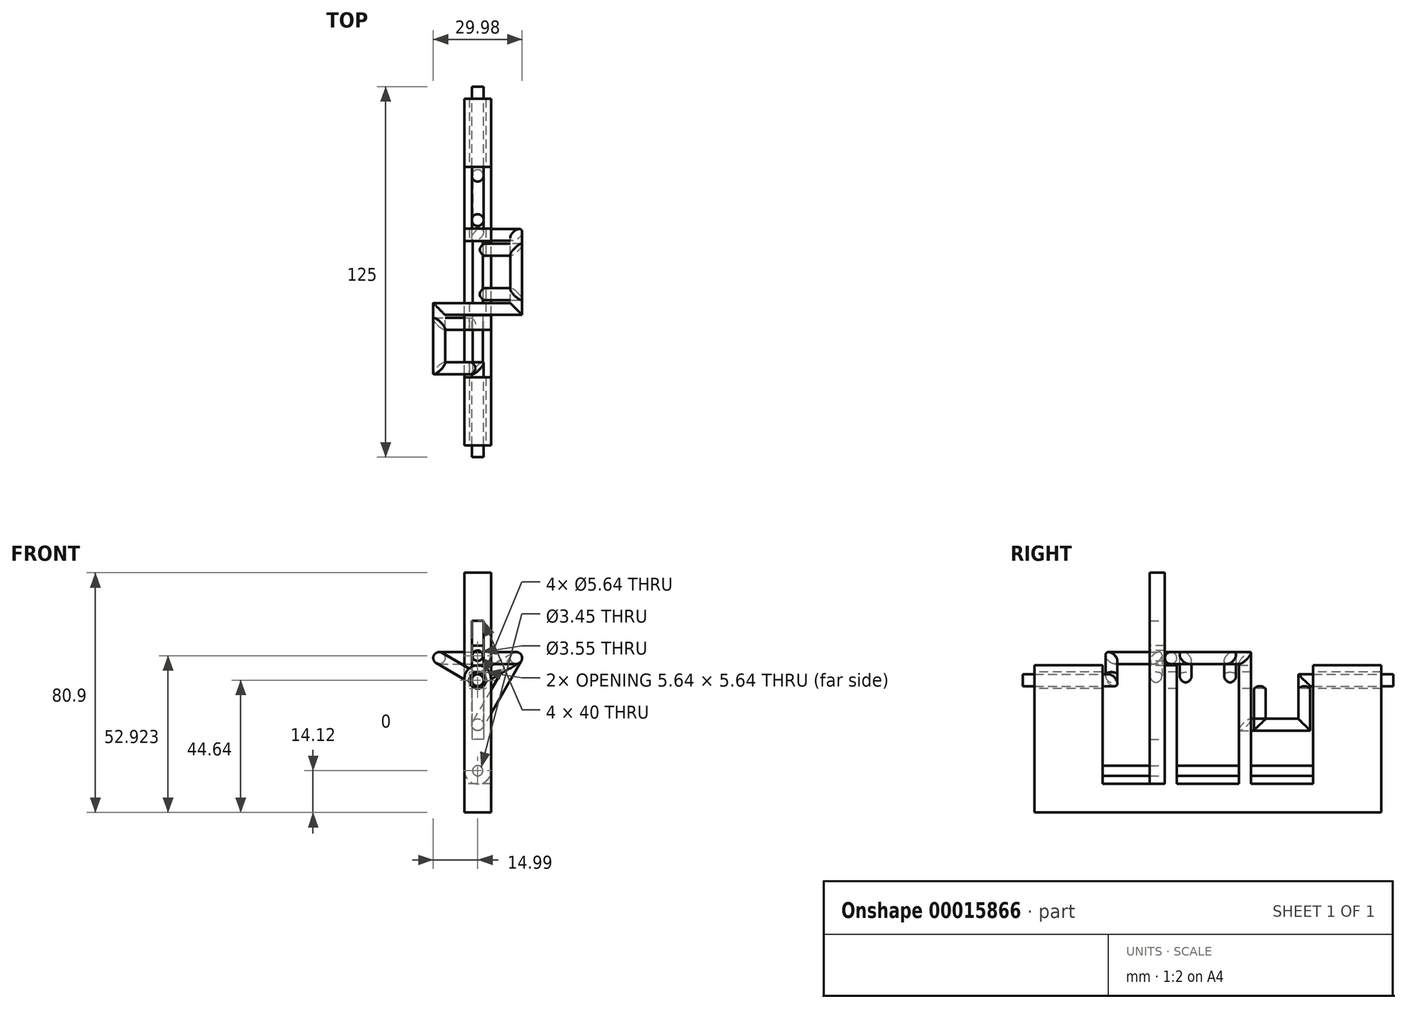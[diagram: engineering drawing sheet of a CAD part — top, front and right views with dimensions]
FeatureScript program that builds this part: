
annotation { "Feature Type Name" : "Feature", "Feature Type Description" : "" }
export const myFeature = defineFeature(function(context is Context, id is Id, definition is map)
    precondition{}
    {
        {
            var Q0;
            Q0=qCreatedBy(makeId("Front.planeOp"),FACE);
            var sketch = newSketch(context, id + "F0", { "sketchPlane" : qUnion([Q0])});
            skCircle(sketch, "E0", {"center": v(0, 0) * mm, "radius": 2 * mm});
            skLineSegment(sketch, "E1", {"start": v(0, 0) * mm, "end": v(-13, 7.5) * mm, "construction": true});
            skLineSegment(sketch, "E2", {"start": v(0, 0) * mm, "end": v(13, 7.5) * mm, "construction": true});
            skLineSegment(sketch, "E3", {"start": v(0, 0) * mm, "end": v(0, -15) * mm, "construction": true});
            skSolve(sketch);
        }
        {
            var Q0;
            Q0=qCreatedBy(makeId("Top.planeOp"),FACE);
            var sketch = newSketch(context, id + "F1", { "sketchPlane" : qUnion([Q0])});
            skLineSegment(sketch, "E4", {"start": v(0, 0) * mm, "end": v(0, 30) * mm});
            skLineSegment(sketch, "E5", {"start": v(0, 45) * mm, "end": v(0, 55) * mm});
            skLineSegment(sketch, "E6", {"start": v(0, 70) * mm, "end": v(0, 80) * mm});
            skLineSegment(sketch, "E7", {"start": v(0, 95) * mm, "end": v(0, 125) * mm});
            skLineSegment(sketch, "E8", {"start": v(0, 30) * mm, "end": v(0, 45) * mm, "construction": true});
            skLineSegment(sketch, "E9", {"start": v(0, 55) * mm, "end": v(0, 70) * mm, "construction": true});
            skLineSegment(sketch, "E10", {"start": v(0, 80) * mm, "end": v(0, 95) * mm, "construction": true});
            skSolve(sketch);
        }
        {
            var Q0;
            Q0=sQuery(id+"F0.wireOp",VERTEX,"E1.end");
            var Q1;
            Q1=sQuery(id+"F0.wireOp",VERTEX,"E2.start");
            var Q2;
            Q2=sQuery(id+"F1.wireOp",VERTEX,"E8.start");
            cPlane(context, id + "F2", {"entities" : qUnion([Q0, Q1, Q2]), "cplaneType" : CPlaneType.THREE_POINT, "offset" : 150 * mm, "width" : 150 * mm, "height" : 150 * mm});
        }
        {
            var Q0;
            Q0=sQuery(id+"F0.wireOp",VERTEX,"E2.end");
            var Q1;
            Q1=sQuery(id+"F0.wireOp",VERTEX,"E2.start");
            var Q2;
            Q2=sQuery(id+"F1.wireOp",VERTEX,"E8.start");
            cPlane(context, id + "F3", {"entities" : qUnion([Q0, Q1, Q2]), "cplaneType" : CPlaneType.THREE_POINT, "offset" : 150 * mm, "width" : 150 * mm, "height" : 150 * mm});
        }
        {
            var Q0;
            Q0=qCreatedBy(id+"F2.planeOp",FACE);
            var sketch = newSketch(context, id + "F4", { "sketchPlane" : qUnion([Q0])});
            skLineSegment(sketch, "E11.0", {"start": v(0, 0) * mm, "end": v(-15, 0) * mm, "construction": true});
            skLineSegment(sketch, "E12.0", {"start": v(0, -30) * mm, "end": v(0, -45) * mm, "construction": true});
            skLineSegment(sketch, "E13", {"start": v(0, -30) * mm, "end": v(-15, -30) * mm});
            skLineSegment(sketch, "E14", {"start": v(-15, -30) * mm, "end": v(-15, -45) * mm});
            skLineSegment(sketch, "E15", {"start": v(-15, -45) * mm, "end": v(0, -45) * mm});
            skSolve(sketch);
        }
        {
            var Q0;
            Q0=qCreatedBy(id+"F3.planeOp",FACE);
            var sketch = newSketch(context, id + "F5", { "sketchPlane" : qUnion([Q0])});
            skLineSegment(sketch, "E16.0", {"start": v(0, 0) * mm, "end": v(15, 0) * mm, "construction": true});
            skLineSegment(sketch, "E16.1", {"start": v(0, 55) * mm, "end": v(0, 70) * mm, "construction": true});
            skLineSegment(sketch, "E17", {"start": v(0, 55) * mm, "end": v(15, 55) * mm});
            skLineSegment(sketch, "E18", {"start": v(15, 55) * mm, "end": v(15, 70) * mm});
            skLineSegment(sketch, "E19", {"start": v(15, 70) * mm, "end": v(0, 70) * mm});
            skSolve(sketch);
        }
        {
            var Q0;
            Q0=qCreatedBy(makeId("Right.planeOp"),FACE);
            var sketch = newSketch(context, id + "F6", { "sketchPlane" : qUnion([Q0])});
            skLineSegment(sketch, "E20.0", {"start": v(0, 0) * mm, "end": v(0, -15) * mm, "construction": true});
            skLineSegment(sketch, "E20.1", {"start": v(80, 0) * mm, "end": v(95, 0) * mm, "construction": true});
            skLineSegment(sketch, "E21", {"start": v(80, 0) * mm, "end": v(80, -15) * mm});
            skLineSegment(sketch, "E22", {"start": v(80, -15) * mm, "end": v(95, -15) * mm});
            skLineSegment(sketch, "E23", {"start": v(95, -15) * mm, "end": v(95, 0) * mm});
            skSolve(sketch);
        }
        {
            var Q0;
            Q0=makeQuery(id+"F0.imprint","IMPRINT",FACE,{"disambiguationData":[TD([[makeQuery(id+"F0.imprint","IMPRINT",EDGE,{"derivedFrom":sQuery(id+"F0.wireOp",EDGE,"E0")}),1.0]])]});
            var Q1;
            Q1=sQuery(id+"F1.wireOp",EDGE,"E4");
            var Q2;
            Q2=sQuery(id+"F4.wireOp",EDGE,"E13");
            var Q3;
            Q3=sQuery(id+"F4.wireOp",EDGE,"E14");
            var Q4;
            Q4=sQuery(id+"F4.wireOp",EDGE,"E15");
            var Q5;
            Q5=sQuery(id+"F1.wireOp",EDGE,"E5");
            var Q6;
            Q6=sQuery(id+"F5.wireOp",EDGE,"E17");
            var Q7;
            Q7=sQuery(id+"F5.wireOp",EDGE,"E19");
            var Q8;
            Q8=sQuery(id+"F5.wireOp",EDGE,"E18");
            var Q9;
            Q9=sQuery(id+"F1.wireOp",EDGE,"E6");
            var Q10;
            Q10=sQuery(id+"F6.wireOp",EDGE,"E21");
            var Q11;
            Q11=sQuery(id+"F6.wireOp",EDGE,"E22");
            var Q12;
            Q12=sQuery(id+"F6.wireOp",EDGE,"E23");
            var Q13;
            Q13=sQuery(id+"F1.wireOp",EDGE,"E7");
            sweep(context, id + "F7", {"profiles" : qUnion([Q0]), "path" : qUnion([Q1, Q2, Q3, Q4, Q5, Q6, Q7, Q8, Q9, Q10, Q11, Q12, Q13])});
        }
        {
            var Q0;
            Q0=qCreatedBy(makeId("Right.planeOp"),FACE);
            var sketch = newSketch(context, id + "F8", { "sketchPlane" : qUnion([Q0])});
            skLineSegment(sketch, "E24", {"start": v(4, -44.64) * mm, "end": v(4, 5) * mm});
            skLineSegment(sketch, "E25", {"start": v(4, 5) * mm, "end": v(27, 5) * mm});
            skLineSegment(sketch, "E26", {"start": v(27, 5) * mm, "end": v(27, -35) * mm});
            skLineSegment(sketch, "E27", {"start": v(27, -35) * mm, "end": v(47.92, -35) * mm});
            skLineSegment(sketch, "E28", {"start": v(47.92, -35) * mm, "end": v(47.92, 5) * mm});
            skLineSegment(sketch, "E29", {"start": v(47.92, 5) * mm, "end": v(52.04, 5) * mm});
            skLineSegment(sketch, "E30", {"start": v(52.04, 5) * mm, "end": v(52.04, -35) * mm});
            skLineSegment(sketch, "E31", {"start": v(52.04, -35) * mm, "end": v(72.96, -35) * mm});
            skLineSegment(sketch, "E32", {"start": v(72.96, -35) * mm, "end": v(72.96, 5) * mm});
            skLineSegment(sketch, "E33", {"start": v(72.96, 5) * mm, "end": v(77.08, 5) * mm});
            skLineSegment(sketch, "E34", {"start": v(77.08, 5) * mm, "end": v(77.08, -35) * mm});
            skLineSegment(sketch, "E35", {"start": v(77.08, -35) * mm, "end": v(98, -35) * mm});
            skLineSegment(sketch, "E36", {"start": v(98, -35) * mm, "end": v(98, 5) * mm});
            skLineSegment(sketch, "E37", {"start": v(98, 5) * mm, "end": v(121, 5) * mm});
            skLineSegment(sketch, "E38", {"start": v(121, 5) * mm, "end": v(121, -44.64) * mm});
            skLineSegment(sketch, "E39", {"start": v(121, -44.64) * mm, "end": v(4, -44.64) * mm});
            skSolve(sketch);
        }
        {
            var Q0;
            Q0=makeQuery(id+"F8.imprint","IMPRINT",FACE,{"disambiguationData":[TD([[makeQuery(id+"F8.imprint","IMPRINT",EDGE,{"derivedFrom":sQuery(id+"F8.wireOp",EDGE,"E24")}),-1.0]])]});
            extrude(context, id + "F9", {"entities" : qUnion([Q0]), "endBound" : BoundingType.SYMMETRIC, "depth" : 9 * mm});
        }
        {
            var Q0;
            Q0=makeQuery(id+"F9.opExtrude","SWEPT_FACE",FACE,{"disambiguationData":[OSD([sQuery(id+"F8.wireOp",EDGE,"E24")])]});
            var sketch = newSketch(context, id + "F10", { "sketchPlane" : qUnion([Q0])});
            skCircle(sketch, "E40", {"center": v(0, 0) * mm, "radius": 2.82 * mm});
            skSolve(sketch);
        }
        {
            var Q0;
            Q0=makeQuery(id+"F9.opExtrude","CAP_FACE",FACE,{"disambiguationData":[OSD([sQuery(id+"F8.wireOp",EDGE,"E24"),sQuery(id+"F8.wireOp",EDGE,"E25"),sQuery(id+"F8.wireOp",EDGE,"E26"),sQuery(id+"F8.wireOp",EDGE,"E27"),sQuery(id+"F8.wireOp",EDGE,"E28"),sQuery(id+"F8.wireOp",EDGE,"E29"),sQuery(id+"F8.wireOp",EDGE,"E30"),sQuery(id+"F8.wireOp",EDGE,"E31"),sQuery(id+"F8.wireOp",EDGE,"E32"),sQuery(id+"F8.wireOp",EDGE,"E33"),sQuery(id+"F8.wireOp",EDGE,"E34"),sQuery(id+"F8.wireOp",EDGE,"E35"),sQuery(id+"F8.wireOp",EDGE,"E36"),sQuery(id+"F8.wireOp",EDGE,"E37"),sQuery(id+"F8.wireOp",EDGE,"E38"),sQuery(id+"F8.wireOp",EDGE,"E39")])],"isStart":false});
            var sketch = newSketch(context, id + "F11", { "sketchPlane" : qUnion([Q0])});
            skLineSegment(sketch, "E41.0.0", {"start": v(4, 5) * mm, "end": v(4, -44.64) * mm});
            skLineSegment(sketch, "E41.0.1", {"start": v(4, -44.64) * mm, "end": v(121, -44.64) * mm});
            skLineSegment(sketch, "E41.0.2", {"start": v(121, -44.64) * mm, "end": v(121, 5) * mm});
            skLineSegment(sketch, "E41.0.3", {"start": v(121, 5) * mm, "end": v(98, 5) * mm});
            skLineSegment(sketch, "E41.0.4", {"start": v(98, 5) * mm, "end": v(98, -35) * mm});
            skLineSegment(sketch, "E41.0.5", {"start": v(98, -35) * mm, "end": v(77.08, -35) * mm});
            skLineSegment(sketch, "E41.0.6", {"start": v(77.08, -35) * mm, "end": v(77.08, 5) * mm});
            skLineSegment(sketch, "E41.0.7", {"start": v(77.08, 5) * mm, "end": v(72.96, 5) * mm});
            skLineSegment(sketch, "E41.0.8", {"start": v(72.96, 5) * mm, "end": v(72.96, -35) * mm});
            skLineSegment(sketch, "E41.0.9", {"start": v(72.96, -35) * mm, "end": v(52.04, -35) * mm});
            skLineSegment(sketch, "E41.0.10", {"start": v(52.04, -35) * mm, "end": v(52.04, 5) * mm});
            skLineSegment(sketch, "E41.0.11", {"start": v(52.04, 5) * mm, "end": v(47.92, 5) * mm});
            skLineSegment(sketch, "E41.0.12", {"start": v(47.92, 5) * mm, "end": v(47.92, -35) * mm});
            skLineSegment(sketch, "E41.0.13", {"start": v(47.92, -35) * mm, "end": v(27, -35) * mm});
            skLineSegment(sketch, "E41.0.14", {"start": v(27, -35) * mm, "end": v(27, 5) * mm});
            skLineSegment(sketch, "E41.0.15", {"start": v(27, 5) * mm, "end": v(4, 5) * mm});
            skLineSegment(sketch, "E42", {"start": v(47.92, -35) * mm, "end": v(52.04, -35) * mm});
            skLineSegment(sketch, "E43", {"start": v(72.96, -35) * mm, "end": v(77.08, -35) * mm});
            skSolve(sketch);
        }
        {
            var Q0;
            Q0=makeQuery(id+"F11.imprint","IMPRINT",FACE,{"disambiguationData":[TD([[makeQuery(id+"F11.imprint","IMPRINT",EDGE,{"derivedFrom":sQuery(id+"F11.wireOp",EDGE,"E41.0.0")}),-1.0]])]});
            extrude(context, id + "F12", {"entities" : qUnion([Q0]), "oppositeDirection" : true, "depth" : 9 * mm});
        }
        {
            var Q0;
            Q0=makeQuery(id+"F10.imprint","IMPRINT",FACE,{"disambiguationData":[TD([[makeQuery(id+"F10.imprint","IMPRINT",EDGE,{"derivedFrom":sQuery(id+"F10.wireOp",EDGE,"E40")}),1.0]])]});
            extrude(context, id + "F13", {"entities" : qUnion([Q0]), "operationType" : NewBodyOperationType.REMOVE, "endBound" : BoundingType.THROUGH_ALL, "oppositeDirection" : true, "depth" : 25 * mm});
        }
        {
            var Q0;
            Q0=makeQuery(id+"F9.opExtrude","CAP_EDGE",EDGE,{"disambiguationData":[OSD([sQuery(id+"F8.wireOp",EDGE,"E25")])],"isStart":true});
            var Q1;
            Q1=makeQuery(id+"F9.opExtrude","CAP_EDGE",EDGE,{"disambiguationData":[OSD([sQuery(id+"F8.wireOp",EDGE,"E29")])],"isStart":false});
            var Q2;
            Q2=makeQuery(id+"F9.opExtrude","CAP_EDGE",EDGE,{"disambiguationData":[OSD([sQuery(id+"F8.wireOp",EDGE,"E29")])],"isStart":true});
            var Q3;
            Q3=makeQuery(id+"F9.opExtrude","CAP_EDGE",EDGE,{"disambiguationData":[OSD([sQuery(id+"F8.wireOp",EDGE,"E33")])],"isStart":false});
            var Q4;
            Q4=makeQuery(id+"F9.opExtrude","CAP_EDGE",EDGE,{"disambiguationData":[OSD([sQuery(id+"F8.wireOp",EDGE,"E33")])],"isStart":true});
            var Q5;
            Q5=makeQuery(id+"F9.opExtrude","CAP_EDGE",EDGE,{"disambiguationData":[OSD([sQuery(id+"F8.wireOp",EDGE,"E37")])],"isStart":false});
            var Q6;
            Q6=makeQuery(id+"F9.opExtrude","CAP_EDGE",EDGE,{"disambiguationData":[OSD([sQuery(id+"F8.wireOp",EDGE,"E37")])],"isStart":true});
            var Q7;
            Q7=makeQuery(id+"F9.opExtrude","CAP_EDGE",EDGE,{"disambiguationData":[OSD([sQuery(id+"F8.wireOp",EDGE,"E25")])],"isStart":false});
            var Q8;
            Q8=makeQuery(id+"F12.opExtrude","CAP_EDGE",EDGE,{"disambiguationData":[OSD([sQuery(id+"F11.wireOp",EDGE,"E41.0.15")])],"isStart":true});
            var Q9;
            Q9=makeQuery(id+"F12.opExtrude","CAP_EDGE",EDGE,{"disambiguationData":[OSD([sQuery(id+"F11.wireOp",EDGE,"E41.0.15")])],"isStart":false});
            var Q10;
            Q10=makeQuery(id+"F12.opExtrude","CAP_EDGE",EDGE,{"disambiguationData":[OSD([sQuery(id+"F11.wireOp",EDGE,"E41.0.3")])],"isStart":true});
            var Q11;
            Q11=makeQuery(id+"F12.opExtrude","CAP_EDGE",EDGE,{"disambiguationData":[OSD([sQuery(id+"F11.wireOp",EDGE,"E41.0.3")])],"isStart":false});
            fillet(context, id + "F14", {"entities" : qUnion([Q0, Q1, Q2, Q3, Q4, Q5, Q6, Q7, Q8, Q9, Q10, Q11]), "radius" : 4.5 * mm, "tangentPropagation" : true, "allowEdgeOverflow" : false});
        }
        {
            var Q0;
            Q0=qCreatedBy(id+"F2.planeOp",FACE);
            var sketch = newSketch(context, id + "F15", { "sketchPlane" : qUnion([Q0])});
            skLineSegment(sketch, "E44.0", {"start": v(0, -45) * mm, "end": v(0, -55) * mm, "construction": true});
            skLineSegment(sketch, "E44.1", {"start": v(0, 0) * mm, "end": v(-15, 0) * mm, "construction": true});
            skLineSegment(sketch, "E45.0", {"start": v(0, -30) * mm, "end": v(0, -45) * mm, "construction": true});
            skLineSegment(sketch, "E46", {"start": v(0, -30) * mm, "end": v(-15, -30) * mm});
            skLineSegment(sketch, "E47", {"start": v(0, -50) * mm, "end": v(-15, -50) * mm, "construction": true});
            skLineSegment(sketch, "E48", {"start": v(-15, -50) * mm, "end": v(-15, -30) * mm});
            skSolve(sketch);
        }
        {
            var Q0;
            Q0=qCreatedBy(id+"F3.planeOp",FACE);
            var sketch = newSketch(context, id + "F16", { "sketchPlane" : qUnion([Q0])});
            skLineSegment(sketch, "E49.0", {"start": v(0, 0) * mm, "end": v(15, 0) * mm, "construction": true});
            skPoint(sketch, "E49.1", {"position": v(0, 50) * mm});
            skLineSegment(sketch, "E49.2", {"start": v(0, 70) * mm, "end": v(0, 80) * mm, "construction": true});
            skLineSegment(sketch, "E50", {"start": v(0, 75) * mm, "end": v(15, 75) * mm, "construction": true});
            skLineSegment(sketch, "E51", {"start": v(15, 75) * mm, "end": v(15, 50) * mm});
            skSolve(sketch);
        }
        {
            var Q0;
            Q0=sQuery(id+"F16.wireOp",VERTEX,"E50.end");
            var Q1;
            Q1=sQuery(id+"F16.wireOp",VERTEX,"E51.end");
            var Q2;
            Q2=sQuery(id+"F15.wireOp",VERTEX,"E47.end");
            cPlane(context, id + "F17", {"entities" : qUnion([Q0, Q1, Q2]), "cplaneType" : CPlaneType.THREE_POINT, "offset" : 150 * mm, "width" : 150 * mm, "height" : 150 * mm});
        }
        {
            var Q0;
            Q0=qCreatedBy(id+"F17.planeOp",FACE);
            var sketch = newSketch(context, id + "F18", { "sketchPlane" : qUnion([Q0])});
            skPoint(sketch, "E52.0", {"position": v(13, 50) * mm});
            skPoint(sketch, "E52.1", {"position": v(-13, 50) * mm});
            skLineSegment(sketch, "E53", {"start": v(-13, 50) * mm, "end": v(13, 50) * mm});
            skSolve(sketch);
        }
        {
            var Q0;
            Q0=sQuery(id+"F6.wireOp",VERTEX,"E22.end");
            var Q1;
            Q1=sQuery(id+"F6.wireOp",VERTEX,"E22.start");
            var Q2;
            Q2=sQuery(id+"F16.wireOp",VERTEX,"E51.start");
            cPlane(context, id + "F19", {"entities" : qUnion([Q0, Q1, Q2]), "cplaneType" : CPlaneType.THREE_POINT, "offset" : 150 * mm, "width" : 150 * mm, "height" : 150 * mm});
        }
        {
            var Q0;
            Q0=qCreatedBy(id+"F19.planeOp",FACE);
            var sketch = newSketch(context, id + "F20", { "sketchPlane" : qUnion([Q0])});
            skPoint(sketch, "E54.0", {"position": v(95, -13) * mm});
            skPoint(sketch, "E54.1", {"position": v(75, 13) * mm});
            skLineSegment(sketch, "E55", {"start": v(75, 13) * mm, "end": v(75, -13) * mm});
            skLineSegment(sketch, "E56", {"start": v(75, -13) * mm, "end": v(95, -13) * mm});
            skSolve(sketch);
        }
        {
            var Q0;
            Q0=makeQuery(id+"F0.imprint","IMPRINT",FACE,{"disambiguationData":[TD([[makeQuery(id+"F0.imprint","IMPRINT",EDGE,{"derivedFrom":sQuery(id+"F0.wireOp",EDGE,"E0")}),1.0]])]});
            var Q1;
            Q1=sQuery(id+"F1.wireOp",EDGE,"E4");
            var Q2;
            Q2=sQuery(id+"F15.wireOp",EDGE,"E46");
            var Q3;
            Q3=sQuery(id+"F15.wireOp",EDGE,"E48");
            var Q4;
            Q4=sQuery(id+"F18.wireOp",EDGE,"E53");
            var Q5;
            Q5=sQuery(id+"F16.wireOp",EDGE,"E51");
            var Q6;
            Q6=sQuery(id+"F20.wireOp",EDGE,"E55");
            var Q7;
            Q7=sQuery(id+"F20.wireOp",EDGE,"E56");
            var Q8;
            Q8=sQuery(id+"F6.wireOp",EDGE,"E23");
            var Q9;
            Q9=sQuery(id+"F1.wireOp",EDGE,"E7");
            sweep(context, id + "F21", {"profiles" : qUnion([Q0]), "path" : qUnion([Q1, Q2, Q3, Q4, Q5, Q6, Q7, Q8, Q9])});
        }
        {
            var Q0;
            Q0=makeQuery(id+"F9.opExtrude","SWEPT_FACE",FACE,{"disambiguationData":[OSD([sQuery(id+"F8.wireOp",EDGE,"E26")])]});
            var sketch = newSketch(context, id + "F22", { "sketchPlane" : qUnion([Q0])});
            skCircle(sketch, "E57", {"center": v(0, -30.52) * mm, "radius": 1.73 * mm});
            skSolve(sketch);
        }
        {
            var Q0;
            Q0=makeQuery(id+"F22.imprint","IMPRINT",FACE,{"disambiguationData":[TD([[makeQuery(id+"F22.imprint","IMPRINT",EDGE,{"derivedFrom":sQuery(id+"F22.wireOp",EDGE,"E57")}),1.0]])]});
            extrude(context, id + "F23", {"entities" : qUnion([Q0]), "operationType" : NewBodyOperationType.ADD, "depth" : 75 * mm});
        }
        {
            var Q0;
            Q0=makeQuery(id+"F9.opExtrude","SWEPT_FACE",FACE,{"disambiguationData":[OSD([sQuery(id+"F8.wireOp",EDGE,"E28")])]});
            var sketch = newSketch(context, id + "F24", { "sketchPlane" : qUnion([Q0])});
            skCircle(sketch, "E58.0", {"center": v(0, -30.52) * mm, "radius": 1.73 * mm});
            skArc(sketch, "E59", {"start": v(-4.5, -30.52) * mm, "mid": v(0, -35.02) * mm, "end": v(4.5, -30.52) * mm});
            skLineSegment(sketch, "E60", {"start": v(-4.5, -30.52) * mm, "end": v(-4.5, 36.26) * mm});
            skLineSegment(sketch, "E61", {"start": v(-4.5, 36.26) * mm, "end": v(4.5, 36.26) * mm});
            skLineSegment(sketch, "E62", {"start": v(4.5, 36.26) * mm, "end": v(4.5, -30.52) * mm});
            skCircle(sketch, "E63.0", {"center": v(0, 0) * mm, "radius": 2 * mm, "construction": true});
            skLineSegment(sketch, "E64", {"start": v(-2, 20) * mm, "end": v(-2, -20) * mm});
            skLineSegment(sketch, "E65", {"start": v(2, 20) * mm, "end": v(2, -20) * mm});
            skLineSegment(sketch, "E66", {"start": v(2, -20) * mm, "end": v(-2, -20) * mm});
            skLineSegment(sketch, "E67", {"start": v(-2, 20) * mm, "end": v(2, 20) * mm});
            skSolve(sketch);
        }
        {
            var Q0;
            Q0=qSketchRegion(id+"F24",true);
            extrude(context, id + "F25", {"entities" : qUnion([Q0]), "depth" : 5 * mm});
        }
        {
            var Q0;
            Q0=makeQuery(id+"F25.opExtrude","CAP_FACE",FACE,{"disambiguationData":[OSD([sQuery(id+"F24.wireOp",EDGE,"E58.0"),sQuery(id+"F24.wireOp",EDGE,"E59"),sQuery(id+"F24.wireOp",EDGE,"E60"),sQuery(id+"F24.wireOp",EDGE,"E61"),sQuery(id+"F24.wireOp",EDGE,"E62"),sQuery(id+"F24.wireOp",EDGE,"E64"),sQuery(id+"F24.wireOp",EDGE,"E65"),sQuery(id+"F24.wireOp",EDGE,"E66"),sQuery(id+"F24.wireOp",EDGE,"E67")])],"isStart":false});
            var sketch = newSketch(context, id + "F26", { "sketchPlane" : qUnion([Q0])});
            skLineSegment(sketch, "E68.bottom", {"start": v(-2, 4.95) * mm, "end": v(2, 4.95) * mm});
            skLineSegment(sketch, "E68.top", {"start": v(-2, 11.61) * mm, "end": v(2, 11.61) * mm});
            skLineSegment(sketch, "E68.left", {"start": v(-2, 4.95) * mm, "end": v(-2, 11.61) * mm});
            skLineSegment(sketch, "E68.right", {"start": v(2, 4.95) * mm, "end": v(2, 11.61) * mm});
            skLineSegment(sketch, "E69", {"start": v(-2, 8.28) * mm, "end": v(0, 8.28) * mm, "construction": true});
            skCircle(sketch, "E70", {"center": v(0, 8.28) * mm, "radius": 1.78 * mm});
            skSolve(sketch);
        }
        {
            var Q0;
            Q0=makeQuery(id+"F26.imprint","IMPRINT",FACE,{"disambiguationData":[TD([[makeQuery(id+"F26.imprint","IMPRINT",EDGE,{"derivedFrom":sQuery(id+"F26.wireOp",EDGE,"E68.bottom")}),1.0]])]});
            extrude(context, id + "F27", {"entities" : qUnion([Q0]), "oppositeDirection" : true, "depth" : 5 * mm});
        }
    });
